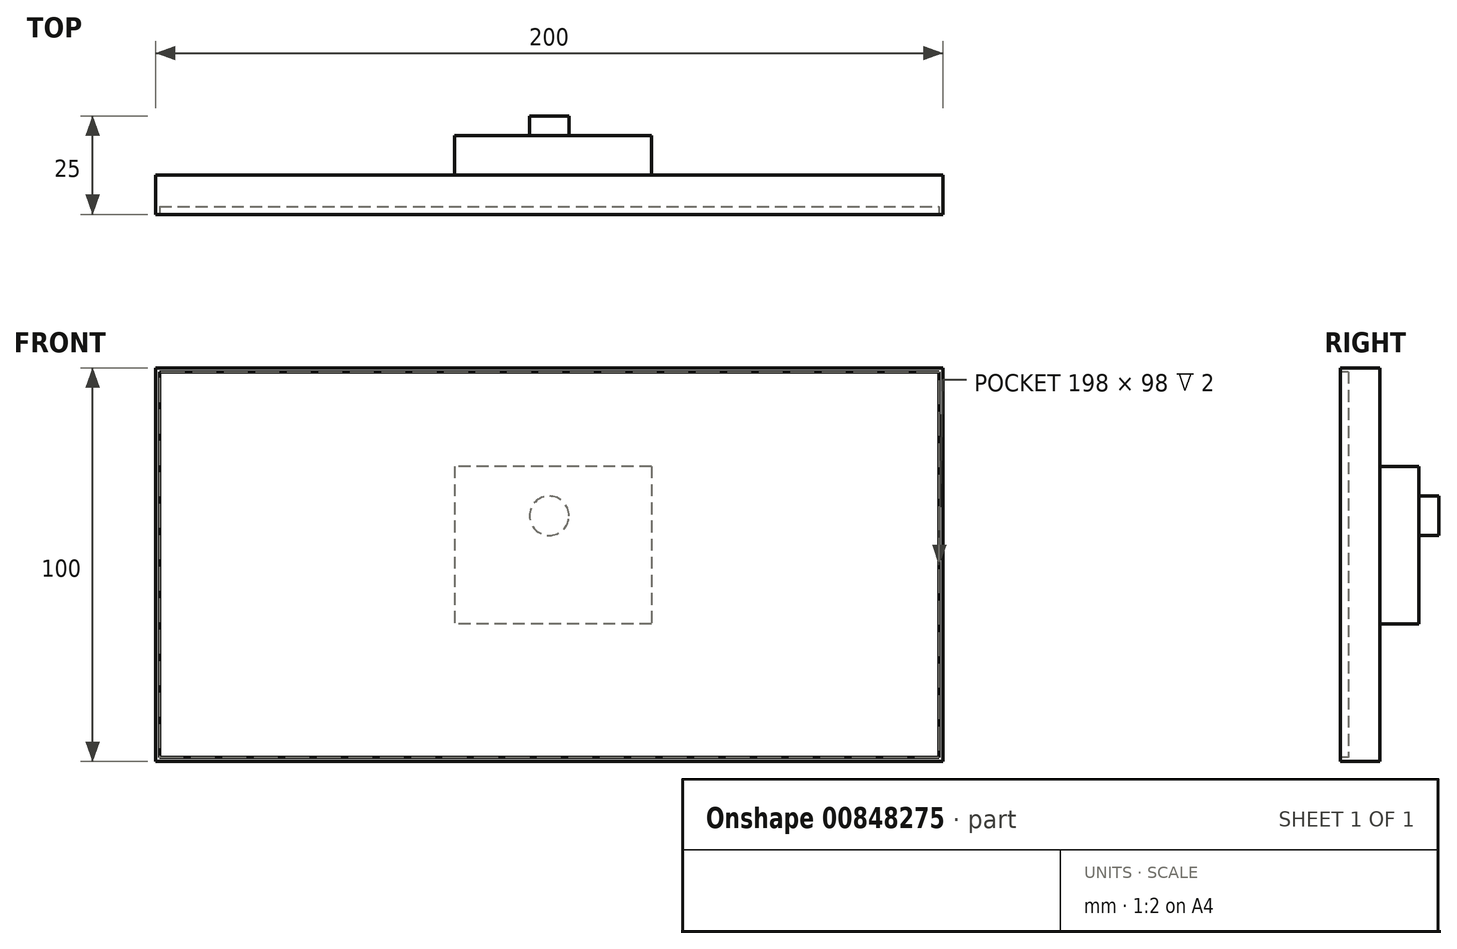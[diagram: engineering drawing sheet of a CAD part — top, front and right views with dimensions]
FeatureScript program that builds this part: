
annotation { "Feature Type Name" : "Feature", "Feature Type Description" : "" }
export const myFeature = defineFeature(function(context is Context, id is Id, definition is map)
    precondition{}
    {
        {
            var Q0;
            Q0=qCreatedBy(makeId("Front.planeOp"),FACE);
            var sketch = newSketch(context, id + "F0", { "sketchPlane" : qUnion([Q0])});
            skLineSegment(sketch, "E0.bottom", {"start": v(-100, 37.59) * mm, "end": v(100, 37.59) * mm});
            skLineSegment(sketch, "E0.top", {"start": v(-100, -62.41) * mm, "end": v(100, -62.41) * mm});
            skLineSegment(sketch, "E0.left", {"start": v(-100, 37.59) * mm, "end": v(-100, -62.41) * mm});
            skLineSegment(sketch, "E0.right", {"start": v(100, 37.59) * mm, "end": v(100, -62.41) * mm});
            skSolve(sketch);
        }
        {
            var Q0;
            Q0 = qSketchRegion(id + "F0", true);
            extrude(context, id + "F1", {"entities" : qUnion([Q0]), "depth" : 10 * mm, "offsetDistance" : 25 * mm});
        }
        {
            var Q0;
            Q0=makeQuery(id+"F1.opExtrude","CAP_FACE",FACE,{"disambiguationData":[OSD([sQuery(id+"F0.wireOp",EDGE,"E0.bottom"),sQuery(id+"F0.wireOp",EDGE,"E0.top"),sQuery(id+"F0.wireOp",EDGE,"E0.left"),sQuery(id+"F0.wireOp",EDGE,"E0.right")])],"isStart":false});
            var sketch = newSketch(context, id + "F2", { "sketchPlane" : qUnion([Q0])});
            skLineSegment(sketch, "E1.bottom", {"start": v(-99, 36.59) * mm, "end": v(99, 36.59) * mm});
            skLineSegment(sketch, "E1.top", {"start": v(-99, -61.41) * mm, "end": v(99, -61.41) * mm});
            skLineSegment(sketch, "E1.left", {"start": v(-99, 36.59) * mm, "end": v(-99, -61.41) * mm});
            skLineSegment(sketch, "E1.right", {"start": v(99, 36.59) * mm, "end": v(99, -61.41) * mm});
            skSolve(sketch);
        }
        {
            var Q0;
            Q0=makeQuery(id+"F2.imprint","IMPRINT",FACE,{"disambiguationData":[TD([[makeQuery(id+"F2.imprint","IMPRINT",EDGE,{"derivedFrom":sQuery(id+"F2.wireOp",EDGE,"E1.bottom")}),-1.0]])]});
            extrude(context, id + "F3", {"entities" : qUnion([Q0]), "operationType" : NewBodyOperationType.REMOVE, "oppositeDirection" : true, "depth" : 2 * mm, "offsetDistance" : 25 * mm});
        }
        {
            var Q0;
            Q0=makeQuery(id+"F1.opExtrude","CAP_FACE",FACE,{"disambiguationData":[OSD([sQuery(id+"F0.wireOp",EDGE,"E0.bottom"),sQuery(id+"F0.wireOp",EDGE,"E0.top"),sQuery(id+"F0.wireOp",EDGE,"E0.left"),sQuery(id+"F0.wireOp",EDGE,"E0.right")])],"isStart":true});
            var sketch = newSketch(context, id + "F4", { "sketchPlane" : qUnion([Q0])});
            skLineSegment(sketch, "E2.bottom", {"start": v(-25.96, 12.59) * mm, "end": v(24.04, 12.59) * mm});
            skLineSegment(sketch, "E2.top", {"start": v(-25.96, -27.41) * mm, "end": v(24.04, -27.41) * mm});
            skLineSegment(sketch, "E2.left", {"start": v(-25.96, 12.59) * mm, "end": v(-25.96, -27.41) * mm});
            skLineSegment(sketch, "E2.right", {"start": v(24.04, 12.59) * mm, "end": v(24.04, -27.41) * mm});
            skSolve(sketch);
        }
        {
            var Q0;
            Q0=makeQuery(id+"F4.imprint","IMPRINT",FACE,{"disambiguationData":[TD([[makeQuery(id+"F4.imprint","IMPRINT",EDGE,{"derivedFrom":sQuery(id+"F4.wireOp",EDGE,"E2.bottom")}),-1.0]])]});
            extrude(context, id + "F5", {"entities" : qUnion([Q0]), "operationType" : NewBodyOperationType.ADD, "depth" : 10 * mm, "offsetDistance" : 25 * mm});
        }
        {
            var Q0;
            Q0=makeQuery(id+"F5.opExtrude","CAP_FACE",FACE,{"disambiguationData":[OSD([sQuery(id+"F4.wireOp",EDGE,"E2.bottom"),sQuery(id+"F4.wireOp",EDGE,"E2.top"),sQuery(id+"F4.wireOp",EDGE,"E2.left"),sQuery(id+"F4.wireOp",EDGE,"E2.right")])],"isStart":false});
            var sketch = newSketch(context, id + "F6", { "sketchPlane" : qUnion([Q0])});
            skCircle(sketch, "E3", {"center": v(0, 0) * mm, "radius": 5 * mm});
            skSolve(sketch);
        }
        {
            var Q0;
            Q0 = qSketchRegion(id + "F6", true);
            extrude(context, id + "F7", {"entities" : qUnion([Q0]), "operationType" : NewBodyOperationType.ADD, "depth" : 5 * mm, "offsetDistance" : 25 * mm});
        }
    });
